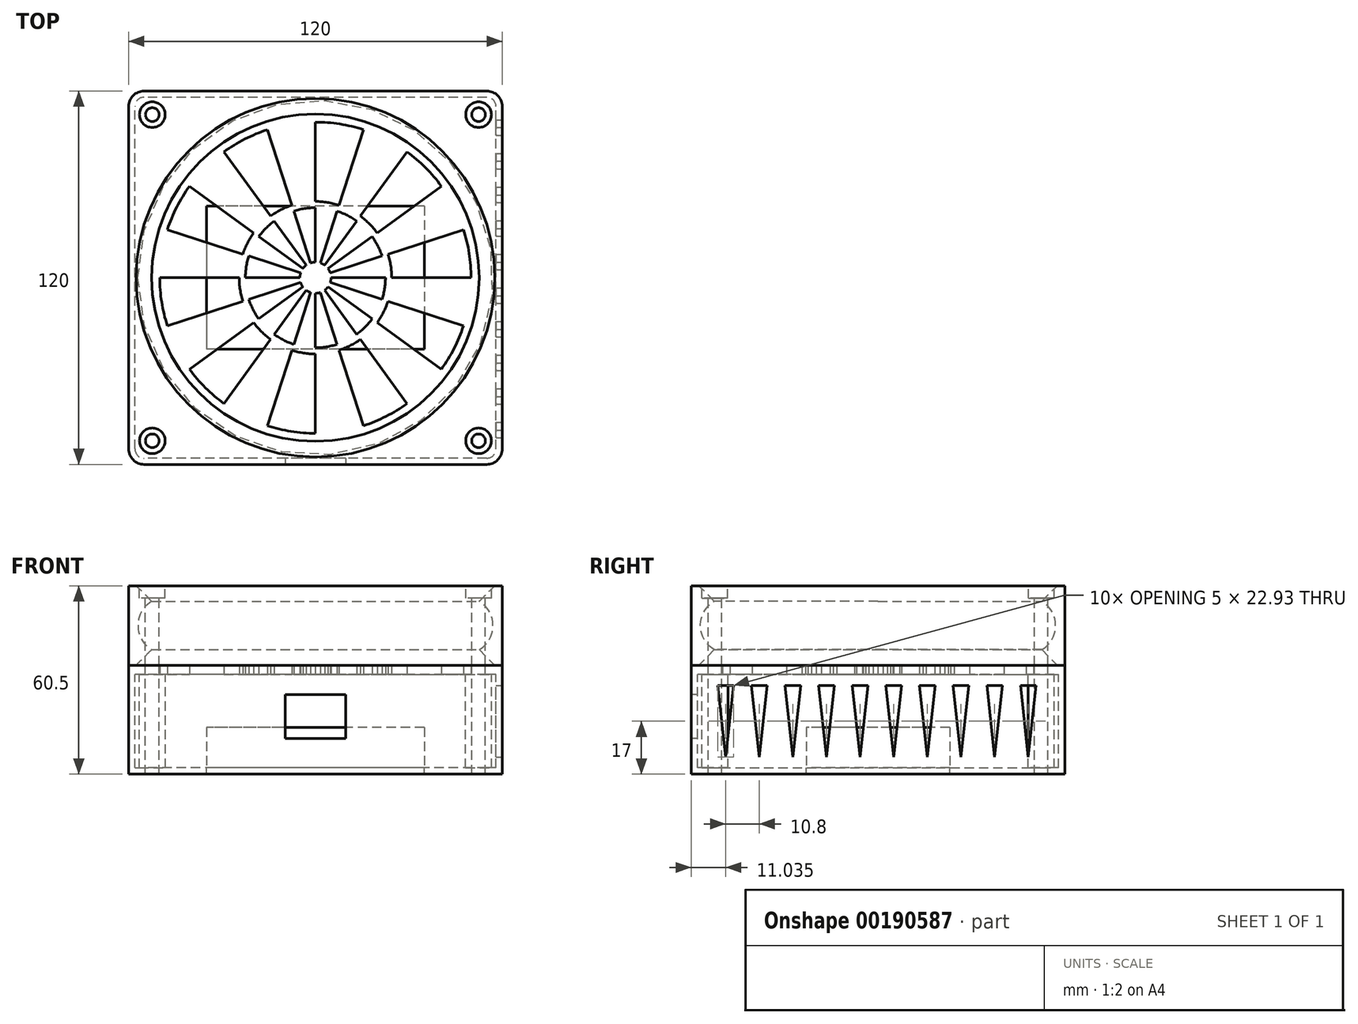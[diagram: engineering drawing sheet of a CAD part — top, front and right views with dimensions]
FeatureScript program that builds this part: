
annotation { "Feature Type Name" : "Feature", "Feature Type Description" : "" }
export const myFeature = defineFeature(function(context is Context, id is Id, definition is map)
    precondition{}
    {
        {
            var Q0;
            Q0=qCreatedBy(makeId("Top.planeOp"),FACE);
            var sketch = newSketch(context, id + "F0", { "sketchPlane" : qUnion([Q0])});
            skLineSegment(sketch, "E0.bottom", {"start": v(60, -60) * mm, "end": v(-60, -60) * mm});
            skLineSegment(sketch, "E0.top", {"start": v(60, 60) * mm, "end": v(-60, 60) * mm});
            skLineSegment(sketch, "E0.left", {"start": v(60, -60) * mm, "end": v(60, 60) * mm});
            skLineSegment(sketch, "E0.right", {"start": v(-60, -60) * mm, "end": v(-60, 60) * mm});
            skPoint(sketch, "E0.middle", {"position": v(0, 0) * mm});
            skPoint(sketch, "E1", {"position": v(-52.4, 52.4) * mm});
            skPoint(sketch, "E2", {"position": v(-52.4, -52.4) * mm});
            skPoint(sketch, "E3", {"position": v(52.4, -52.4) * mm});
            skPoint(sketch, "E4", {"position": v(52.4, 52.4) * mm});
            skLineSegment(sketch, "E5", {"start": v(-52.4, 52.4) * mm, "end": v(52.4, 52.4) * mm, "construction": true});
            skLineSegment(sketch, "E6", {"start": v(-52.4, 52.4) * mm, "end": v(-52.4, -52.4) * mm, "construction": true});
            skLineSegment(sketch, "E7", {"start": v(-52.4, -52.4) * mm, "end": v(52.4, -52.4) * mm, "construction": true});
            skLineSegment(sketch, "E8", {"start": v(52.4, -52.4) * mm, "end": v(52.4, 52.4) * mm, "construction": true});
            skLineSegment(sketch, "E9", {"start": v(-60, 60) * mm, "end": v(60, -60) * mm, "construction": true});
            skLineSegment(sketch, "E10", {"start": v(-60, -60) * mm, "end": v(60, 60) * mm, "construction": true});
            skCircle(sketch, "E11", {"center": v(0, 0) * mm, "radius": 52.6 * mm});
            skSolve(sketch);
        }
        {
            var Q0;
            Q0=makeQuery(id+"F0.imprint","IMPRINT",FACE,{"disambiguationData":[TD([[makeQuery(id+"F0.imprint","IMPRINT",EDGE,{"derivedFrom":sQuery(id+"F0.wireOp",EDGE,"E0.bottom")}),-1.0]])]});
            extrude(context, id + "F1", {"entities" : qUnion([Q0]), "oppositeDirection" : true, "depth" : 25.5 * mm});
        }
        {
            var Q0;
            Q0=makeQuery(id+"F1.opExtrude","SWEPT_FACE",FACE,{"disambiguationData":[OSD([sQuery(id+"F0.wireOp",EDGE,"E11")])]});
            chamfer(context, id + "F2", {"entities" : qUnion([Q0]), "width" : 5 * mm, "tangentPropagation" : true});
        }
        {
            var Q0;
            Q0=qCreatedBy(makeId("Front.planeOp"),FACE);
            var sketch = newSketch(context, id + "F3", { "sketchPlane" : qUnion([Q0])});
            skLineSegment(sketch, "E12", {"start": v(-52.6, -5) * mm, "end": v(-52.6, -20.5) * mm});
            skLineSegment(sketch, "E13", {"start": v(52.6, -20.5) * mm, "end": v(52.6, -5) * mm});
            skArc(sketch, "E14", {"start": v(-52.6, -5) * mm, "mid": v(-57.03, -12.75) * mm, "end": v(-52.6, -20.5) * mm});
            skSolve(sketch);
        }
        {
            var Q0;
            Q0=makeQuery(id+"F3.imprint","IMPRINT",FACE,{"disambiguationData":[TD([[makeQuery(id+"F3.imprint","IMPRINT",EDGE,{"derivedFrom":sQuery(id+"F3.wireOp",EDGE,"E12")}),-1.0]])]});
            var Q1;
            Q1=makeQuery(id+"F1.opExtrude","SWEPT_FACE",FACE,{"disambiguationData":[OSD([sQuery(id+"F0.wireOp",EDGE,"E11")])]});
            revolve(context, id + "F4", {"operationType" : NewBodyOperationType.REMOVE, "entities" : qUnion([Q0]), "axis" : qUnion([Q1]), "revolveType" : RevolveType.FULL, "oppositeDirection" : true});
        }
        {
            var Q0;
            Q0=makeQuery(id+"F1.opExtrude","SWEPT_EDGE",EDGE,{"disambiguationData":[OSD([sQuery(id+"F0.wireOp",EDGE,"E0.bottom"),sQuery(id+"F0.wireOp",EDGE,"E0.right")])]});
            var Q1;
            Q1=makeQuery(id+"F1.opExtrude","SWEPT_EDGE",EDGE,{"disambiguationData":[OSD([sQuery(id+"F0.wireOp",EDGE,"E0.bottom"),sQuery(id+"F0.wireOp",EDGE,"E0.left")])]});
            var Q2;
            Q2=makeQuery(id+"F1.opExtrude","SWEPT_EDGE",EDGE,{"disambiguationData":[OSD([sQuery(id+"F0.wireOp",EDGE,"E0.top"),sQuery(id+"F0.wireOp",EDGE,"E0.left")])]});
            var Q3;
            Q3=makeQuery(id+"F1.opExtrude","SWEPT_EDGE",EDGE,{"disambiguationData":[OSD([sQuery(id+"F0.wireOp",EDGE,"E0.top"),sQuery(id+"F0.wireOp",EDGE,"E0.right")])]});
            fillet(context, id + "F5", {"entities" : qUnion([Q0, Q1, Q2, Q3]), "radius" : 5 * mm, "tangentPropagation" : true, "allowEdgeOverflow" : false});
        }
        {
            var Q0;
            Q0=makeQuery(id+"F1.opExtrude","CAP_FACE",FACE,{"disambiguationData":[OSD([sQuery(id+"F0.wireOp",EDGE,"E0.bottom"),sQuery(id+"F0.wireOp",EDGE,"E0.top"),sQuery(id+"F0.wireOp",EDGE,"E0.left"),sQuery(id+"F0.wireOp",EDGE,"E0.right"),sQuery(id+"F0.wireOp",EDGE,"E11")])],"isStart":false});
            var sketch = newSketch(context, id + "F6", { "sketchPlane" : qUnion([Q0])});
            skSolve(sketch);
        }
        {
            var Q0;
            {var subQ0=sQuery(id+"F0.wireOp",EDGE,"E11");Q0=makeQuery(id+"F6.imprint","IMPRINT",FACE,{"disambiguationData":[TD([[makeQuery(id+"F6.imprint","IMPRINT",EDGE,{"derivedFrom":makeQuery(id+"F2.opChamfer","BLEND_EDGE",EDGE,{"blendedFrom":[makeQuery(id+"F1.opExtrude","CAP_EDGE",EDGE,{"disambiguationData":[OSD([subQ0])],"isStart":false}),makeQuery(id+"F1.opExtrude","CAP_FACE",FACE,{"disambiguationData":[OSD([sQuery(id+"F0.wireOp",EDGE,"E0.bottom"),sQuery(id+"F0.wireOp",EDGE,"E0.top"),sQuery(id+"F0.wireOp",EDGE,"E0.left"),sQuery(id+"F0.wireOp",EDGE,"E0.right"),subQ0])],"isStart":false})],"blendedInto":[makeQuery(id+"F1.opExtrude","CAP_FACE",FACE,{"disambiguationData":[OSD([sQuery(id+"F0.wireOp",EDGE,"E0.bottom"),sQuery(id+"F0.wireOp",EDGE,"E0.top"),sQuery(id+"F0.wireOp",EDGE,"E0.left"),sQuery(id+"F0.wireOp",EDGE,"E0.right"),subQ0])],"isStart":false})]})}),-1.0]])]});}
            var Q1;
            {var subQ4=sQuery(id+"F0.wireOp",EDGE,"E0.bottom");Q1=makeQuery(id+"F6.imprint","IMPRINT",FACE,{"disambiguationData":[TD([[makeQuery(id+"F6.imprint","IMPRINT",EDGE,{"derivedFrom":makeQuery(id+"F1.opExtrude","CAP_EDGE",EDGE,{"disambiguationData":[OSD([subQ4])],"isStart":false})}),1.0]])]});}
            extrude(context, id + "F7", {"entities" : qUnion([Q0, Q1]), "depth" : 3 * mm});
        }
        {
            var Q0;
            Q0=makeQuery(id+"F7.opExtrude","CAP_FACE",FACE,{"disambiguationData":[OSD([sQuery(id+"F0.wireOp",EDGE,"E0.bottom"),sQuery(id+"F0.wireOp",EDGE,"E0.top"),sQuery(id+"F0.wireOp",EDGE,"E0.left"),sQuery(id+"F0.wireOp",EDGE,"E0.right"),sQuery(id+"F0.wireOp",EDGE,"E11"),sQuery(id+"F14.hole-0.sketch.wireOp",EDGE,"core_line_2"),sQuery(id+"F14.hole-1.sketch.wireOp",EDGE,"core_line_2"),sQuery(id+"F14.hole-2.sketch.wireOp",EDGE,"core_line_2"),sQuery(id+"F14.hole-3.sketch.wireOp",EDGE,"core_line_2")])],"isStart":false});
            var sketch = newSketch(context, id + "F8", { "sketchPlane" : qUnion([Q0])});
            skArc(sketch, "E15.0", {"start": v(58, 55) * mm, "mid": v(57.12, 57.12) * mm, "end": v(55, 58) * mm});
            skLineSegment(sketch, "E15.1", {"start": v(55, 58) * mm, "end": v(-55, 58) * mm});
            skLineSegment(sketch, "E15.2", {"start": v(58, 55) * mm, "end": v(58, -55) * mm});
            skArc(sketch, "E15.3", {"start": v(-55, 58) * mm, "mid": v(-57.12, 57.12) * mm, "end": v(-58, 55) * mm});
            skArc(sketch, "E15.4", {"start": v(55, -58) * mm, "mid": v(57.12, -57.12) * mm, "end": v(58, -55) * mm});
            skLineSegment(sketch, "E15.5", {"start": v(55, -58) * mm, "end": v(-55, -58) * mm});
            skArc(sketch, "E15.6", {"start": v(-58, -55) * mm, "mid": v(-57.12, -57.12) * mm, "end": v(-55, -58) * mm});
            skLineSegment(sketch, "E15.7", {"start": v(-58, 55) * mm, "end": v(-58, -55) * mm});
            skPoint(sketch, "E16.0", {"position": v(0, 0) * mm});
            skCircle(sketch, "E17.0", {"center": v(0, 0) * mm, "radius": 52.6 * mm});
            skCircle(sketch, "E18", {"center": v(0, 0) * mm, "radius": 5 * mm});
            skCircle(sketch, "E19", {"center": v(0, 0) * mm, "radius": 50 * mm});
            skCircle(sketch, "E20", {"center": v(0, 0) * mm, "radius": 22.5 * mm});
            skLineSegment(sketch, "E21", {"start": v(-5, 0) * mm, "end": v(-50, 0) * mm});
            skLineSegment(sketch, "E22.1.0", {"start": v(-4.76, -1.55) * mm, "end": v(-47.55, -15.45) * mm});
            skLineSegment(sketch, "E22.2.0", {"start": v(-4.05, -2.94) * mm, "end": v(-40.45, -29.39) * mm});
            skLineSegment(sketch, "E22.3.0", {"start": v(-2.94, -4.05) * mm, "end": v(-29.39, -40.45) * mm});
            skLineSegment(sketch, "E22.4.0", {"start": v(-1.55, -4.76) * mm, "end": v(-15.45, -47.55) * mm});
            skLineSegment(sketch, "E22.5.0", {"start": v(0, -5) * mm, "end": v(0, -50) * mm});
            skLineSegment(sketch, "E22.6.0", {"start": v(1.55, -4.76) * mm, "end": v(15.45, -47.55) * mm});
            skLineSegment(sketch, "E22.7.0", {"start": v(2.94, -4.05) * mm, "end": v(29.39, -40.45) * mm});
            skLineSegment(sketch, "E22.8.0", {"start": v(4.05, -2.94) * mm, "end": v(40.45, -29.39) * mm});
            skLineSegment(sketch, "E22.9.0", {"start": v(4.76, -1.55) * mm, "end": v(47.55, -15.45) * mm});
            skLineSegment(sketch, "E22.10.0", {"start": v(5, 0) * mm, "end": v(50, 0) * mm});
            skLineSegment(sketch, "E22.11.0", {"start": v(4.76, 1.55) * mm, "end": v(47.55, 15.45) * mm});
            skLineSegment(sketch, "E22.12.0", {"start": v(4.05, 2.94) * mm, "end": v(40.45, 29.39) * mm});
            skLineSegment(sketch, "E22.13.0", {"start": v(2.94, 4.05) * mm, "end": v(29.39, 40.45) * mm});
            skLineSegment(sketch, "E22.14.0", {"start": v(1.55, 4.76) * mm, "end": v(15.45, 47.55) * mm});
            skLineSegment(sketch, "E22.15.0", {"start": v(0, 5) * mm, "end": v(0, 50) * mm});
            skLineSegment(sketch, "E22.16.0", {"start": v(-1.55, 4.76) * mm, "end": v(-15.45, 47.55) * mm});
            skLineSegment(sketch, "E22.17.0", {"start": v(-2.94, 4.05) * mm, "end": v(-29.39, 40.45) * mm});
            skLineSegment(sketch, "E22.18.0", {"start": v(-4.05, 2.94) * mm, "end": v(-40.45, 29.39) * mm});
            skLineSegment(sketch, "E22.19.0", {"start": v(-4.76, 1.55) * mm, "end": v(-47.55, 15.45) * mm});
            skCircle(sketch, "E23.0", {"center": v(0, 0) * mm, "radius": 24.5 * mm});
            skSolve(sketch);
        }
        {
            var Q0;
            Q0=makeQuery(id+"F8.imprint","IMPRINT",FACE,{"disambiguationData":[TD([[makeQuery(id+"F8.imprint","IMPRINT",EDGE,{"derivedFrom":sQuery(id+"F8.wireOp",EDGE,"E15.0")}),-1.0]])]});
            extrude(context, id + "F9", {"entities" : qUnion([Q0]), "operationType" : NewBodyOperationType.ADD, "depth" : 30 * mm});
        }
        {
            var Q0;
            {var subQ0=sQuery(id+"F8.wireOp",EDGE,"E22.16.0");var subQ1=sQuery(id+"F8.wireOp",EDGE,"E18");var subQ2=makeQuery(id+"F8.imprint","INTERSECT",VERTEX,{"derivedFrom":[subQ1,subQ0]});Q0=makeQuery(id+"F8.imprint","IMPRINT",FACE,{"disambiguationData":[TD([[makeQuery(id+"F8.imprint","IMPRINT",EDGE,{"disambiguationData":[TD([[subQ2,-1.0]])],"derivedFrom":subQ1}),-1.0]])]});}
            var Q1;
            {var subQ0=sQuery(id+"F8.wireOp",EDGE,"E22.14.0");var subQ1=sQuery(id+"F8.wireOp",EDGE,"E18");var subQ2=makeQuery(id+"F8.imprint","INTERSECT",VERTEX,{"derivedFrom":[subQ1,subQ0]});Q1=makeQuery(id+"F8.imprint","IMPRINT",FACE,{"disambiguationData":[TD([[makeQuery(id+"F8.imprint","IMPRINT",EDGE,{"disambiguationData":[TD([[subQ2,-1.0]])],"derivedFrom":subQ1}),-1.0]])]});}
            var Q2;
            {var subQ0=sQuery(id+"F8.wireOp",EDGE,"E22.12.0");var subQ1=sQuery(id+"F8.wireOp",EDGE,"E18");var subQ2=makeQuery(id+"F8.imprint","INTERSECT",VERTEX,{"derivedFrom":[subQ1,subQ0]});Q2=makeQuery(id+"F8.imprint","IMPRINT",FACE,{"disambiguationData":[TD([[makeQuery(id+"F8.imprint","IMPRINT",EDGE,{"disambiguationData":[TD([[subQ2,-1.0]])],"derivedFrom":subQ1}),-1.0]])]});}
            var Q3;
            {var subQ0=sQuery(id+"F8.wireOp",EDGE,"E22.10.0");var subQ1=sQuery(id+"F8.wireOp",EDGE,"E18");var subQ2=makeQuery(id+"F8.imprint","INTERSECT",VERTEX,{"derivedFrom":[subQ1,subQ0]});Q3=makeQuery(id+"F8.imprint","IMPRINT",FACE,{"disambiguationData":[TD([[makeQuery(id+"F8.imprint","IMPRINT",EDGE,{"disambiguationData":[TD([[subQ2,-1.0]])],"derivedFrom":subQ1}),-1.0]])]});}
            var Q4;
            {var subQ0=sQuery(id+"F8.wireOp",EDGE,"E22.8.0");var subQ1=sQuery(id+"F8.wireOp",EDGE,"E18");var subQ2=makeQuery(id+"F8.imprint","INTERSECT",VERTEX,{"derivedFrom":[subQ1,subQ0]});Q4=makeQuery(id+"F8.imprint","IMPRINT",FACE,{"disambiguationData":[TD([[makeQuery(id+"F8.imprint","IMPRINT",EDGE,{"disambiguationData":[TD([[subQ2,-1.0]])],"derivedFrom":subQ1}),-1.0]])]});}
            var Q5;
            {var subQ0=sQuery(id+"F8.wireOp",EDGE,"E22.6.0");var subQ1=sQuery(id+"F8.wireOp",EDGE,"E18");var subQ2=makeQuery(id+"F8.imprint","INTERSECT",VERTEX,{"derivedFrom":[subQ1,subQ0]});Q5=makeQuery(id+"F8.imprint","IMPRINT",FACE,{"disambiguationData":[TD([[makeQuery(id+"F8.imprint","IMPRINT",EDGE,{"disambiguationData":[TD([[subQ2,-1.0]])],"derivedFrom":subQ1}),-1.0]])]});}
            var Q6;
            {var subQ0=sQuery(id+"F8.wireOp",EDGE,"E22.4.0");var subQ1=sQuery(id+"F8.wireOp",EDGE,"E18");var subQ2=makeQuery(id+"F8.imprint","INTERSECT",VERTEX,{"derivedFrom":[subQ1,subQ0]});Q6=makeQuery(id+"F8.imprint","IMPRINT",FACE,{"disambiguationData":[TD([[makeQuery(id+"F8.imprint","IMPRINT",EDGE,{"disambiguationData":[TD([[subQ2,-1.0]])],"derivedFrom":subQ1}),-1.0]])]});}
            var Q7;
            {var subQ0=sQuery(id+"F8.wireOp",EDGE,"E22.2.0");var subQ1=sQuery(id+"F8.wireOp",EDGE,"E18");var subQ2=makeQuery(id+"F8.imprint","INTERSECT",VERTEX,{"derivedFrom":[subQ1,subQ0]});Q7=makeQuery(id+"F8.imprint","IMPRINT",FACE,{"disambiguationData":[TD([[makeQuery(id+"F8.imprint","IMPRINT",EDGE,{"disambiguationData":[TD([[subQ2,-1.0]])],"derivedFrom":subQ1}),-1.0]])]});}
            var Q8;
            {var subQ0=sQuery(id+"F8.wireOp",EDGE,"E21");var subQ1=sQuery(id+"F8.wireOp",EDGE,"E18");var subQ2=makeQuery(id+"F8.imprint","INTERSECT",VERTEX,{"derivedFrom":[subQ1,subQ0]});Q8=makeQuery(id+"F8.imprint","IMPRINT",FACE,{"disambiguationData":[TD([[makeQuery(id+"F8.imprint","IMPRINT",EDGE,{"disambiguationData":[TD([[subQ2,-1.0]])],"derivedFrom":subQ1}),-1.0]])]});}
            var Q9;
            {var subQ0=sQuery(id+"F8.wireOp",EDGE,"E22.18.0");var subQ1=sQuery(id+"F8.wireOp",EDGE,"E18");var subQ2=makeQuery(id+"F8.imprint","INTERSECT",VERTEX,{"derivedFrom":[subQ1,subQ0]});Q9=makeQuery(id+"F8.imprint","IMPRINT",FACE,{"disambiguationData":[TD([[makeQuery(id+"F8.imprint","IMPRINT",EDGE,{"disambiguationData":[TD([[subQ2,-1.0]])],"derivedFrom":subQ1}),-1.0]])]});}
            var Q10;
            {var subQ0=sQuery(id+"F8.wireOp",EDGE,"E22.17.0");var subQ1=sQuery(id+"F8.wireOp",EDGE,"E19");var subQ2=makeQuery(id+"F8.imprint","INTERSECT",VERTEX,{"derivedFrom":[subQ1,subQ0]});Q10=makeQuery(id+"F8.imprint","IMPRINT",FACE,{"disambiguationData":[TD([[makeQuery(id+"F8.imprint","IMPRINT",EDGE,{"disambiguationData":[TD([[subQ2,-1.0]])],"derivedFrom":subQ1}),1.0]])]});}
            var Q11;
            {var subQ0=sQuery(id+"F8.wireOp",EDGE,"E22.15.0");var subQ1=sQuery(id+"F8.wireOp",EDGE,"E19");var subQ2=makeQuery(id+"F8.imprint","INTERSECT",VERTEX,{"derivedFrom":[subQ1,subQ0]});Q11=makeQuery(id+"F8.imprint","IMPRINT",FACE,{"disambiguationData":[TD([[makeQuery(id+"F8.imprint","IMPRINT",EDGE,{"disambiguationData":[TD([[subQ2,-1.0]])],"derivedFrom":subQ1}),1.0]])]});}
            var Q12;
            {var subQ0=sQuery(id+"F8.wireOp",EDGE,"E22.13.0");var subQ1=sQuery(id+"F8.wireOp",EDGE,"E19");var subQ2=makeQuery(id+"F8.imprint","INTERSECT",VERTEX,{"derivedFrom":[subQ1,subQ0]});Q12=makeQuery(id+"F8.imprint","IMPRINT",FACE,{"disambiguationData":[TD([[makeQuery(id+"F8.imprint","IMPRINT",EDGE,{"disambiguationData":[TD([[subQ2,-1.0]])],"derivedFrom":subQ1}),1.0]])]});}
            var Q13;
            {var subQ0=sQuery(id+"F8.wireOp",EDGE,"E22.11.0");var subQ1=sQuery(id+"F8.wireOp",EDGE,"E19");var subQ2=makeQuery(id+"F8.imprint","INTERSECT",VERTEX,{"derivedFrom":[subQ1,subQ0]});Q13=makeQuery(id+"F8.imprint","IMPRINT",FACE,{"disambiguationData":[TD([[makeQuery(id+"F8.imprint","IMPRINT",EDGE,{"disambiguationData":[TD([[subQ2,-1.0]])],"derivedFrom":subQ1}),1.0]])]});}
            var Q14;
            {var subQ0=sQuery(id+"F8.wireOp",EDGE,"E22.9.0");var subQ1=sQuery(id+"F8.wireOp",EDGE,"E19");var subQ2=makeQuery(id+"F8.imprint","INTERSECT",VERTEX,{"derivedFrom":[subQ1,subQ0]});Q14=makeQuery(id+"F8.imprint","IMPRINT",FACE,{"disambiguationData":[TD([[makeQuery(id+"F8.imprint","IMPRINT",EDGE,{"disambiguationData":[TD([[subQ2,-1.0]])],"derivedFrom":subQ1}),1.0]])]});}
            var Q15;
            {var subQ0=sQuery(id+"F8.wireOp",EDGE,"E22.7.0");var subQ1=sQuery(id+"F8.wireOp",EDGE,"E19");var subQ2=makeQuery(id+"F8.imprint","INTERSECT",VERTEX,{"derivedFrom":[subQ1,subQ0]});Q15=makeQuery(id+"F8.imprint","IMPRINT",FACE,{"disambiguationData":[TD([[makeQuery(id+"F8.imprint","IMPRINT",EDGE,{"disambiguationData":[TD([[subQ2,-1.0]])],"derivedFrom":subQ1}),1.0]])]});}
            var Q16;
            {var subQ0=sQuery(id+"F8.wireOp",EDGE,"E22.5.0");var subQ1=sQuery(id+"F8.wireOp",EDGE,"E19");var subQ2=makeQuery(id+"F8.imprint","INTERSECT",VERTEX,{"derivedFrom":[subQ1,subQ0]});Q16=makeQuery(id+"F8.imprint","IMPRINT",FACE,{"disambiguationData":[TD([[makeQuery(id+"F8.imprint","IMPRINT",EDGE,{"disambiguationData":[TD([[subQ2,-1.0]])],"derivedFrom":subQ1}),1.0]])]});}
            var Q17;
            {var subQ0=sQuery(id+"F8.wireOp",EDGE,"E22.3.0");var subQ1=sQuery(id+"F8.wireOp",EDGE,"E19");var subQ2=makeQuery(id+"F8.imprint","INTERSECT",VERTEX,{"derivedFrom":[subQ1,subQ0]});Q17=makeQuery(id+"F8.imprint","IMPRINT",FACE,{"disambiguationData":[TD([[makeQuery(id+"F8.imprint","IMPRINT",EDGE,{"disambiguationData":[TD([[subQ2,-1.0]])],"derivedFrom":subQ1}),1.0]])]});}
            var Q18;
            {var subQ0=sQuery(id+"F8.wireOp",EDGE,"E22.1.0");var subQ1=sQuery(id+"F8.wireOp",EDGE,"E19");var subQ2=makeQuery(id+"F8.imprint","INTERSECT",VERTEX,{"derivedFrom":[subQ1,subQ0]});Q18=makeQuery(id+"F8.imprint","IMPRINT",FACE,{"disambiguationData":[TD([[makeQuery(id+"F8.imprint","IMPRINT",EDGE,{"disambiguationData":[TD([[subQ2,-1.0]])],"derivedFrom":subQ1}),1.0]])]});}
            var Q19;
            {var subQ0=sQuery(id+"F8.wireOp",EDGE,"E21");var subQ1=sQuery(id+"F8.wireOp",EDGE,"E19");var subQ2=makeQuery(id+"F8.imprint","INTERSECT",VERTEX,{"derivedFrom":[subQ1,subQ0]});Q19=makeQuery(id+"F8.imprint","IMPRINT",FACE,{"disambiguationData":[TD([[makeQuery(id+"F8.imprint","IMPRINT",EDGE,{"disambiguationData":[TD([[subQ2,1.0]])],"derivedFrom":subQ1}),1.0]])]});}
            extrude(context, id + "F10", {"entities" : qUnion([Q0, Q1, Q2, Q3, Q4, Q5, Q6, Q7, Q8, Q9, Q10, Q11, Q12, Q13, Q14, Q15, Q16, Q17, Q18, Q19]), "operationType" : NewBodyOperationType.REMOVE, "endBound" : BoundingType.UP_TO_NEXT, "oppositeDirection" : true, "depth" : 25 * mm});
        }
        {
            var Q0;
            Q0=makeQuery(id+"F9.opExtrude","CAP_FACE",FACE,{"disambiguationData":[OSD([sQuery(id+"F0.wireOp",EDGE,"E0.bottom"),sQuery(id+"F0.wireOp",EDGE,"E0.top"),sQuery(id+"F0.wireOp",EDGE,"E0.left"),sQuery(id+"F0.wireOp",EDGE,"E0.right"),sQuery(id+"F0.wireOp",EDGE,"E11"),sQuery(id+"F8.wireOp",EDGE,"E15.0"),sQuery(id+"F8.wireOp",EDGE,"E15.1"),sQuery(id+"F8.wireOp",EDGE,"E15.2"),sQuery(id+"F8.wireOp",EDGE,"E15.3"),sQuery(id+"F8.wireOp",EDGE,"E15.4"),sQuery(id+"F8.wireOp",EDGE,"E15.5"),sQuery(id+"F8.wireOp",EDGE,"E15.6"),sQuery(id+"F8.wireOp",EDGE,"E15.7")])],"isStart":false});
            var sketch = newSketch(context, id + "F11", { "sketchPlane" : qUnion([Q0])});
            skLineSegment(sketch, "E24.bottom", {"start": v(35, -23) * mm, "end": v(-35, -23) * mm});
            skLineSegment(sketch, "E24.top", {"start": v(35, 23) * mm, "end": v(-35, 23) * mm});
            skLineSegment(sketch, "E24.left", {"start": v(35, -23) * mm, "end": v(35, 23) * mm});
            skLineSegment(sketch, "E24.right", {"start": v(-35, -23) * mm, "end": v(-35, 23) * mm});
            skPoint(sketch, "E24.middle", {"position": v(0, 0) * mm});
            skSolve(sketch);
        }
        {
            var Q0;
            Q0=makeQuery(id+"F11.imprint","IMPRINT",FACE,{"disambiguationData":[TD([[makeQuery(id+"F11.imprint","IMPRINT",EDGE,{"derivedFrom":sQuery(id+"F11.wireOp",EDGE,"E24.bottom")}),-1.0]])]});
            extrude(context, id + "F12", {"entities" : qUnion([Q0]), "oppositeDirection" : true, "depth" : 13 * mm});
        }
        {
            var Q0;
            Q0=makeQuery(id+"F11.imprint","IMPRINT",FACE,{"disambiguationData":[TD([[makeQuery(id+"F11.imprint","IMPRINT",EDGE,{"derivedFrom":sQuery(id+"F11.wireOp",EDGE,"E24.bottom")}),1.0]])]});
            var Q1;
            Q1=makeQuery(id+"F11.imprint","IMPRINT",FACE,{"disambiguationData":[TD([[makeQuery(id+"F11.imprint","IMPRINT",EDGE,{"derivedFrom":makeQuery(id+"F9.opExtrude","CAP_EDGE",EDGE,{"disambiguationData":[OSD([sQuery(id+"F8.wireOp",EDGE,"E15.0")])],"isStart":false})}),-1.0]])]});
            var Q2;
            Q2=makeQuery(id+"F12.opExtrude","CAP_FACE",FACE,{"disambiguationData":[OSD([sQuery(id+"F11.wireOp",EDGE,"E24.bottom"),sQuery(id+"F11.wireOp",EDGE,"E24.top"),sQuery(id+"F11.wireOp",EDGE,"E24.left"),sQuery(id+"F11.wireOp",EDGE,"E24.right")])],"isStart":true});
            extrude(context, id + "F13", {"entities" : qUnion([Q0, Q1, Q2]), "depth" : 2 * mm});
        }
        {
            var Q0;
            Q0=sQuery(id+"F0.wireOp",VERTEX,"E1");
            var Q1;
            Q1=sQuery(id+"F0.wireOp",VERTEX,"E4");
            var Q2;
            Q2=sQuery(id+"F0.wireOp",VERTEX,"E3");
            var Q3;
            Q3=sQuery(id+"F0.wireOp",VERTEX,"E2");
            var Q4;
            Q4=makeQuery(id+"F1.opExtrude","SWEPT_BODY",BODY,{"disambiguationData":[OSD([sQuery(id+"F0.wireOp",EDGE,"E0.bottom"),sQuery(id+"F0.wireOp",EDGE,"E0.top"),sQuery(id+"F0.wireOp",EDGE,"E0.left"),sQuery(id+"F0.wireOp",EDGE,"E0.right")])]});
            var Q5;
            Q5=makeQuery(id+"F7.opExtrude","SWEPT_BODY",BODY,{"disambiguationData":[OSD([sQuery(id+"F0.wireOp",EDGE,"E0.bottom"),sQuery(id+"F0.wireOp",EDGE,"E0.top"),sQuery(id+"F0.wireOp",EDGE,"E0.left"),sQuery(id+"F0.wireOp",EDGE,"E0.right"),sQuery(id+"F0.wireOp",EDGE,"E11")])]});
            var Q6;
            Q6=makeQuery(id+"F13.opExtrude","SWEPT_BODY",BODY,{"disambiguationData":[OSD([sQuery(id+"F0.wireOp",EDGE,"E0.bottom"),sQuery(id+"F0.wireOp",EDGE,"E0.top"),sQuery(id+"F0.wireOp",EDGE,"E0.left"),sQuery(id+"F0.wireOp",EDGE,"E0.right"),sQuery(id+"F0.wireOp",EDGE,"E11"),sQuery(id+"F11.wireOp",EDGE,"E24.bottom"),sQuery(id+"F11.wireOp",EDGE,"E24.top"),sQuery(id+"F11.wireOp",EDGE,"E24.left"),sQuery(id+"F11.wireOp",EDGE,"E24.right")])]});
            hole(context, id + "F14", {"style" : HoleStyle.C_BORE, "endStyle" : HoleEndStyle.THROUGH, "standardTappedOrClearance" : lookupTablePath({ "standard" : "ISO", "fit" : "Normal", "size" : "M4", "type" : "Clearance" }), "standardBlindInLast" : lookupTablePath({ "fit" : "Standard", "standard" : "ISO", "size" : "M4", "type" : "Clearance" }), "holeDiameter" : 4.4 * mm, "cBoreDiameter" : 8.25 * mm, "cBoreDepth" : 4 * mm, "locations" : qUnion([Q0, Q1, Q2, Q3]), "scope" : qUnion([Q4, Q5, Q6]), "isTappedThrough" : true});
        }
        {
            var Q0;
            {var subQ0=sQuery(id+"F0.wireOp",EDGE,"E0.left");Q0=makeQuery(id+"F9.boolean.opBoolean","MERGE",FACE,{"derivedFrom":[makeQuery(id+"F7.opExtrude","SWEPT_FACE",FACE,{"disambiguationData":[OSD([subQ0])]}),makeQuery(id+"F9.opExtrude","SWEPT_FACE",FACE,{"disambiguationData":[OSD([subQ0])]})]});}
            var sketch = newSketch(context, id + "F15", { "sketchPlane" : qUnion([Q0])});
            skLineSegment(sketch, "E25", {"start": v(-55, -58.5) * mm, "end": v(-51.46, -54.96) * mm, "construction": true});
            skLineSegment(sketch, "E26.0", {"start": v(-55, -28.5) * mm, "end": v(55, -28.5) * mm});
            skLineSegment(sketch, "E27", {"start": v(-55, -28.5) * mm, "end": v(-51.46, -32.04) * mm, "construction": true});
            skLineSegment(sketch, "E28", {"start": v(-51.46, -54.96) * mm, "end": v(55, -54.96) * mm, "construction": true});
            skLineSegment(sketch, "E29", {"start": v(-51.46, -32.04) * mm, "end": v(-46.46, -32.04) * mm});
            skLineSegment(sketch, "E30", {"start": v(-46.46, -32.04) * mm, "end": v(-48.96, -54.96) * mm});
            skLineSegment(sketch, "E31", {"start": v(-48.96, -54.96) * mm, "end": v(-51.46, -32.04) * mm});
            skLineSegment(sketch, "E32.1.0.0", {"start": v(-35.66, -32.04) * mm, "end": v(-38.16, -54.96) * mm});
            skLineSegment(sketch, "E32.1.0.1", {"start": v(-40.66, -32.04) * mm, "end": v(-35.66, -32.04) * mm});
            skLineSegment(sketch, "E32.1.0.2", {"start": v(-38.16, -54.96) * mm, "end": v(-40.66, -32.04) * mm});
            skLineSegment(sketch, "E32.2.0.0", {"start": v(-24.86, -32.04) * mm, "end": v(-27.36, -54.96) * mm});
            skLineSegment(sketch, "E32.2.0.1", {"start": v(-29.86, -32.04) * mm, "end": v(-24.86, -32.04) * mm});
            skLineSegment(sketch, "E32.2.0.2", {"start": v(-27.36, -54.96) * mm, "end": v(-29.86, -32.04) * mm});
            skLineSegment(sketch, "E32.3.0.0", {"start": v(-14.06, -32.04) * mm, "end": v(-16.56, -54.96) * mm});
            skLineSegment(sketch, "E32.3.0.1", {"start": v(-19.06, -32.04) * mm, "end": v(-14.06, -32.04) * mm});
            skLineSegment(sketch, "E32.3.0.2", {"start": v(-16.56, -54.96) * mm, "end": v(-19.06, -32.04) * mm});
            skLineSegment(sketch, "E32.4.0.0", {"start": v(-3.26, -32.04) * mm, "end": v(-5.76, -54.96) * mm});
            skLineSegment(sketch, "E32.4.0.1", {"start": v(-8.26, -32.04) * mm, "end": v(-3.26, -32.04) * mm});
            skLineSegment(sketch, "E32.4.0.2", {"start": v(-5.76, -54.96) * mm, "end": v(-8.26, -32.04) * mm});
            skLineSegment(sketch, "E32.5.0.0", {"start": v(7.54, -32.04) * mm, "end": v(5.04, -54.96) * mm});
            skLineSegment(sketch, "E32.5.0.1", {"start": v(2.54, -32.04) * mm, "end": v(7.54, -32.04) * mm});
            skLineSegment(sketch, "E32.5.0.2", {"start": v(5.04, -54.96) * mm, "end": v(2.54, -32.04) * mm});
            skLineSegment(sketch, "E32.6.0.0", {"start": v(18.34, -32.04) * mm, "end": v(15.84, -54.96) * mm});
            skLineSegment(sketch, "E32.6.0.1", {"start": v(13.34, -32.04) * mm, "end": v(18.34, -32.04) * mm});
            skLineSegment(sketch, "E32.6.0.2", {"start": v(15.84, -54.96) * mm, "end": v(13.34, -32.04) * mm});
            skLineSegment(sketch, "E32.7.0.0", {"start": v(29.14, -32.04) * mm, "end": v(26.64, -54.96) * mm});
            skLineSegment(sketch, "E32.7.0.1", {"start": v(24.14, -32.04) * mm, "end": v(29.14, -32.04) * mm});
            skLineSegment(sketch, "E32.7.0.2", {"start": v(26.64, -54.96) * mm, "end": v(24.14, -32.04) * mm});
            skLineSegment(sketch, "E32.8.0.0", {"start": v(39.94, -32.04) * mm, "end": v(37.44, -54.96) * mm});
            skLineSegment(sketch, "E32.8.0.1", {"start": v(34.94, -32.04) * mm, "end": v(39.94, -32.04) * mm});
            skLineSegment(sketch, "E32.8.0.2", {"start": v(37.44, -54.96) * mm, "end": v(34.94, -32.04) * mm});
            skLineSegment(sketch, "E32.9.0.0", {"start": v(50.74, -32.04) * mm, "end": v(48.24, -54.96) * mm});
            skLineSegment(sketch, "E32.9.0.1", {"start": v(45.74, -32.04) * mm, "end": v(50.74, -32.04) * mm});
            skLineSegment(sketch, "E32.9.0.2", {"start": v(48.24, -54.96) * mm, "end": v(45.74, -32.04) * mm});
            skLineSegment(sketch, "E32.direction1", {"start": v(-48.96, -54.96) * mm, "end": v(-38.16, -54.96) * mm, "construction": true});
            skSolve(sketch);
        }
        {
            var Q0;
            Q0=makeQuery(id+"F15.imprint","IMPRINT",FACE,{"disambiguationData":[TD([[makeQuery(id+"F15.imprint","IMPRINT",EDGE,{"derivedFrom":sQuery(id+"F15.wireOp",EDGE,"E29")}),-1.0]])]});
            var Q1;
            Q1=makeQuery(id+"F15.imprint","IMPRINT",FACE,{"disambiguationData":[TD([[makeQuery(id+"F15.imprint","IMPRINT",EDGE,{"derivedFrom":sQuery(id+"F15.wireOp",EDGE,"E32.1.0.0")}),-1.0]])]});
            var Q2;
            Q2=makeQuery(id+"F15.imprint","IMPRINT",FACE,{"disambiguationData":[TD([[makeQuery(id+"F15.imprint","IMPRINT",EDGE,{"derivedFrom":sQuery(id+"F15.wireOp",EDGE,"E32.2.0.0")}),-1.0]])]});
            var Q3;
            Q3=makeQuery(id+"F15.imprint","IMPRINT",FACE,{"disambiguationData":[TD([[makeQuery(id+"F15.imprint","IMPRINT",EDGE,{"derivedFrom":sQuery(id+"F15.wireOp",EDGE,"E32.3.0.0")}),-1.0]])]});
            var Q4;
            Q4=makeQuery(id+"F15.imprint","IMPRINT",FACE,{"disambiguationData":[TD([[makeQuery(id+"F15.imprint","IMPRINT",EDGE,{"derivedFrom":sQuery(id+"F15.wireOp",EDGE,"E32.4.0.0")}),-1.0]])]});
            var Q5;
            Q5=makeQuery(id+"F15.imprint","IMPRINT",FACE,{"disambiguationData":[TD([[makeQuery(id+"F15.imprint","IMPRINT",EDGE,{"derivedFrom":sQuery(id+"F15.wireOp",EDGE,"E32.5.0.0")}),-1.0]])]});
            var Q6;
            Q6=makeQuery(id+"F15.imprint","IMPRINT",FACE,{"disambiguationData":[TD([[makeQuery(id+"F15.imprint","IMPRINT",EDGE,{"derivedFrom":sQuery(id+"F15.wireOp",EDGE,"E32.6.0.0")}),-1.0]])]});
            var Q7;
            Q7=makeQuery(id+"F15.imprint","IMPRINT",FACE,{"disambiguationData":[TD([[makeQuery(id+"F15.imprint","IMPRINT",EDGE,{"derivedFrom":sQuery(id+"F15.wireOp",EDGE,"E32.7.0.0")}),-1.0]])]});
            var Q8;
            Q8=makeQuery(id+"F15.imprint","IMPRINT",FACE,{"disambiguationData":[TD([[makeQuery(id+"F15.imprint","IMPRINT",EDGE,{"derivedFrom":sQuery(id+"F15.wireOp",EDGE,"E32.8.0.0")}),-1.0]])]});
            var Q9;
            Q9=makeQuery(id+"F15.imprint","IMPRINT",FACE,{"disambiguationData":[TD([[makeQuery(id+"F15.imprint","IMPRINT",EDGE,{"derivedFrom":sQuery(id+"F15.wireOp",EDGE,"E32.9.0.0")}),-1.0]])]});
            extrude(context, id + "F16", {"entities" : qUnion([Q0, Q1, Q2, Q3, Q4, Q5, Q6, Q7, Q8, Q9]), "operationType" : NewBodyOperationType.REMOVE, "endBound" : BoundingType.UP_TO_NEXT, "oppositeDirection" : true, "depth" : 25 * mm});
        }
        {
            var Q0;
            Q0=makeQuery(id+"F8.imprint","IMPRINT",FACE,{"disambiguationData":[TD([[makeQuery(id+"F8.imprint","IMPRINT",EDGE,{"derivedFrom":sQuery(id+"F8.wireOp",EDGE,"E15.0")}),1.0]])]});
            var sketch = newSketch(context, id + "F17", { "sketchPlane" : qUnion([Q0])});
            skCircle(sketch, "E33.0", {"center": v(-52.4, -52.4) * mm, "radius": 2.2 * mm});
            skCircle(sketch, "E33.1", {"center": v(-52.4, 52.4) * mm, "radius": 2.2 * mm});
            skCircle(sketch, "E33.2", {"center": v(52.4, 52.4) * mm, "radius": 2.2 * mm});
            skCircle(sketch, "E33.3", {"center": v(52.4, -52.4) * mm, "radius": 2.2 * mm});
            skCircle(sketch, "E34.0", {"center": v(-52.4, -52.4) * mm, "radius": 4.2 * mm});
            skCircle(sketch, "E35.0", {"center": v(-52.4, 52.4) * mm, "radius": 4.2 * mm});
            skCircle(sketch, "E36.0", {"center": v(52.4, 52.4) * mm, "radius": 4.2 * mm});
            skCircle(sketch, "E37.0", {"center": v(52.4, -52.4) * mm, "radius": 4.2 * mm});
            skSolve(sketch);
        }
        {
            var Q0;
            Q0=makeQuery(id+"F17.imprint","IMPRINT",FACE,{"disambiguationData":[TD([[makeQuery(id+"F17.imprint","IMPRINT",EDGE,{"derivedFrom":sQuery(id+"F17.wireOp",EDGE,"E33.3")}),-1.0]])]});
            var Q1;
            Q1=makeQuery(id+"F17.imprint","IMPRINT",FACE,{"disambiguationData":[TD([[makeQuery(id+"F17.imprint","IMPRINT",EDGE,{"derivedFrom":sQuery(id+"F17.wireOp",EDGE,"E33.2")}),-1.0]])]});
            var Q2;
            Q2=makeQuery(id+"F17.imprint","IMPRINT",FACE,{"disambiguationData":[TD([[makeQuery(id+"F17.imprint","IMPRINT",EDGE,{"derivedFrom":sQuery(id+"F17.wireOp",EDGE,"E33.1")}),-1.0]])]});
            var Q3;
            Q3=makeQuery(id+"F17.imprint","IMPRINT",FACE,{"disambiguationData":[TD([[makeQuery(id+"F17.imprint","IMPRINT",EDGE,{"derivedFrom":sQuery(id+"F17.wireOp",EDGE,"E33.0")}),-1.0]])]});
            extrude(context, id + "F18", {"entities" : qUnion([Q0, Q1, Q2, Q3]), "operationType" : NewBodyOperationType.ADD, "depth" : 30 * mm});
        }
        {
            var Q0;
            {var subQ0=sQuery(id+"F0.wireOp",EDGE,"E0.bottom");Q0=makeQuery(id+"F9.boolean.opBoolean","MERGE",FACE,{"derivedFrom":[makeQuery(id+"F7.opExtrude","SWEPT_FACE",FACE,{"disambiguationData":[OSD([subQ0])]}),makeQuery(id+"F9.opExtrude","SWEPT_FACE",FACE,{"disambiguationData":[OSD([subQ0])]})]});}
            var sketch = newSketch(context, id + "F19", { "sketchPlane" : qUnion([Q0])});
            skLineSegment(sketch, "E38.bottom", {"start": v(9.75, -49) * mm, "end": v(-9.75, -49) * mm});
            skLineSegment(sketch, "E38.top", {"start": v(9.75, -35) * mm, "end": v(-9.75, -35) * mm});
            skLineSegment(sketch, "E38.left", {"start": v(9.75, -49) * mm, "end": v(9.75, -35) * mm});
            skLineSegment(sketch, "E38.right", {"start": v(-9.75, -49) * mm, "end": v(-9.75, -35) * mm});
            skPoint(sketch, "E38.middle", {"position": v(0, -42) * mm});
            skPoint(sketch, "E38.middle.positionSnap0", {"position": v(-55, -42) * mm});
            skPoint(sketch, "E38.centerSnap0", {"position": v(-55, -42) * mm});
            skSolve(sketch);
        }
        {
            var Q0;
            Q0=makeQuery(id+"F19.imprint","IMPRINT",FACE,{"disambiguationData":[TD([[makeQuery(id+"F19.imprint","IMPRINT",EDGE,{"derivedFrom":sQuery(id+"F19.wireOp",EDGE,"E38.bottom")}),-1.0]])]});
            extrude(context, id + "F20", {"entities" : qUnion([Q0]), "operationType" : NewBodyOperationType.REMOVE, "endBound" : BoundingType.UP_TO_NEXT, "oppositeDirection" : true, "depth" : 25 * mm});
        }
    });
